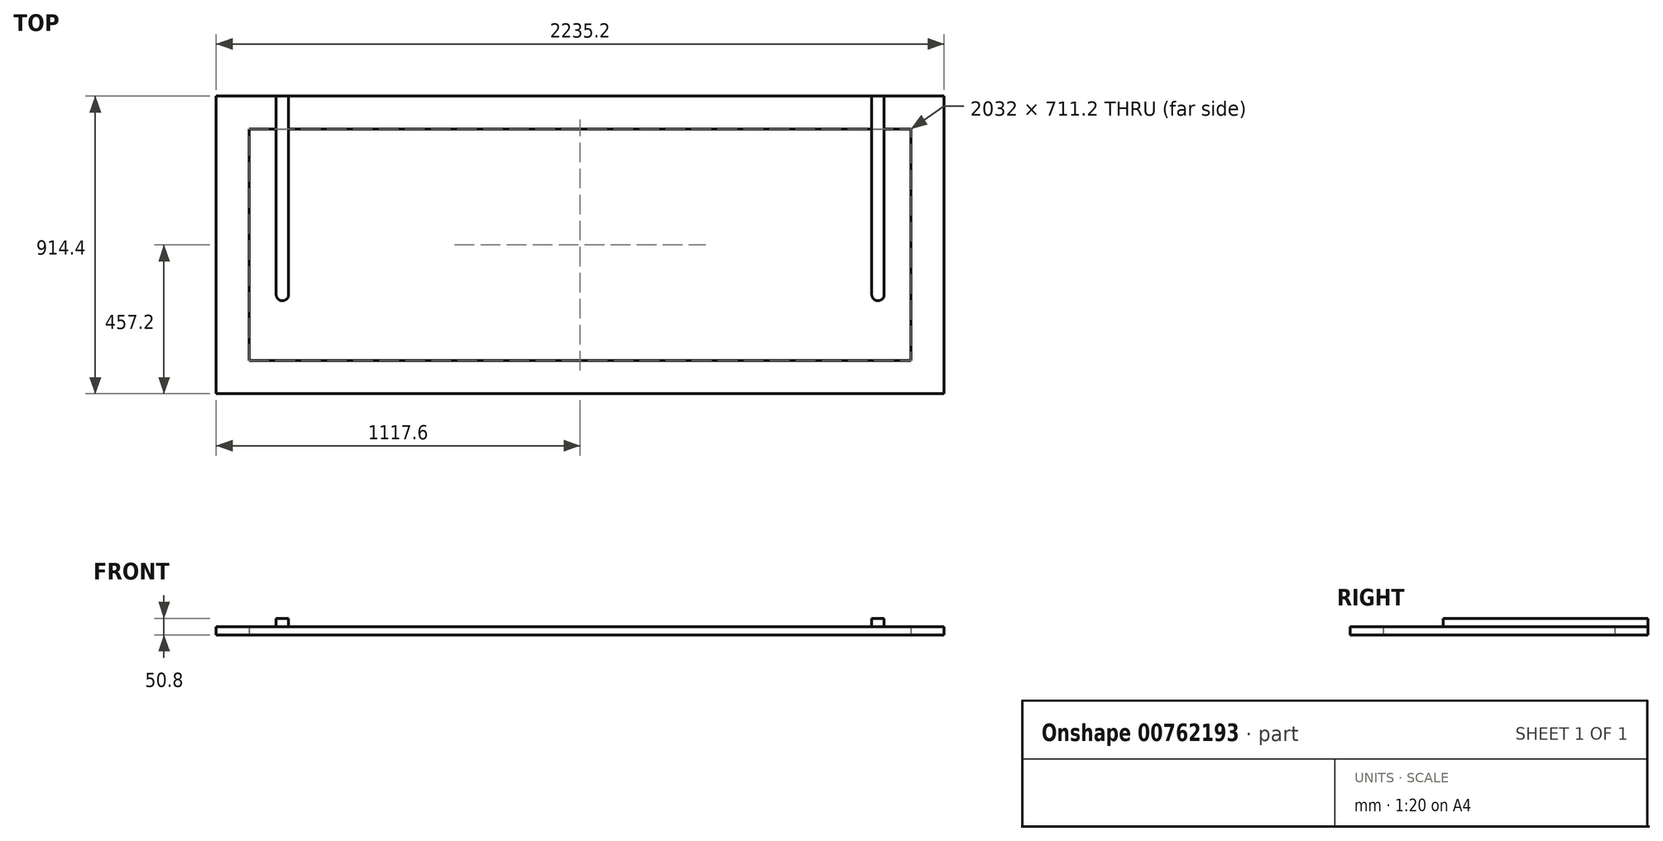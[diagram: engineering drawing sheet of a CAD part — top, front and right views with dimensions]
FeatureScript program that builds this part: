
annotation { "Feature Type Name" : "Feature", "Feature Type Description" : "" }
export const myFeature = defineFeature(function(context is Context, id is Id, definition is map)
    precondition{}
    {
        {
            var Q0;
            Q0=qCreatedBy(makeId("Top.planeOp"),FACE);
            var sketch = newSketch(context, id + "F0", { "sketchPlane" : qUnion([Q0])});
            skLineSegment(sketch, "E0.bottom", {"start": v(0, 0) * mm, "end": v(2235.2, 0) * mm});
            skLineSegment(sketch, "E0.top", {"start": v(0, -914.4) * mm, "end": v(2235.2, -914.4) * mm});
            skLineSegment(sketch, "E0.left", {"start": v(0, 0) * mm, "end": v(0, -914.4) * mm});
            skLineSegment(sketch, "E0.right", {"start": v(2235.2, 0) * mm, "end": v(2235.2, -914.4) * mm});
            skLineSegment(sketch, "E1.bottom", {"start": v(101.6, -101.6) * mm, "end": v(2133.6, -101.6) * mm});
            skLineSegment(sketch, "E1.top", {"start": v(101.6, -812.8) * mm, "end": v(2133.6, -812.8) * mm});
            skLineSegment(sketch, "E1.left", {"start": v(101.6, -101.6) * mm, "end": v(101.6, -812.8) * mm});
            skLineSegment(sketch, "E1.right", {"start": v(2133.6, -101.6) * mm, "end": v(2133.6, -812.8) * mm});
            skSolve(sketch);
        }
        {
            var Q0;
            Q0=makeQuery(id+"F0.imprint","IMPRINT",FACE,{"disambiguationData":[TD([[makeQuery(id+"F0.imprint","IMPRINT",EDGE,{"derivedFrom":sQuery(id+"F0.wireOp",EDGE,"E0.bottom")}),-1.0]])]});
            extrude(context, id + "F1", {"entities" : qUnion([Q0]), "depth" : 25.4 * mm, "offsetDistance" : 25.4 * mm});
        }
        {
            var Q0;
            Q0=makeQuery(id+"F1.opExtrude","CAP_FACE",FACE,{"disambiguationData":[OSD([sQuery(id+"F0.wireOp",EDGE,"E0.bottom"),sQuery(id+"F0.wireOp",EDGE,"E0.top"),sQuery(id+"F0.wireOp",EDGE,"E0.left"),sQuery(id+"F0.wireOp",EDGE,"E0.right"),sQuery(id+"F0.wireOp",EDGE,"E1.bottom"),sQuery(id+"F0.wireOp",EDGE,"E1.top"),sQuery(id+"F0.wireOp",EDGE,"E1.left"),sQuery(id+"F0.wireOp",EDGE,"E1.right")])],"isStart":false});
            var sketch = newSketch(context, id + "F2", { "sketchPlane" : qUnion([Q0])});
            skLineSegment(sketch, "E2.bottom", {"start": v(184.15, 0) * mm, "end": v(222.25, 0) * mm});
            skLineSegment(sketch, "E2.top", {"start": v(184.15, -609.6) * mm, "end": v(222.25, -609.6) * mm});
            skLineSegment(sketch, "E2.left", {"start": v(184.15, 0) * mm, "end": v(184.15, -609.6) * mm});
            skLineSegment(sketch, "E2.right", {"start": v(222.25, 0) * mm, "end": v(222.25, -609.6) * mm});
            skLineSegment(sketch, "E3.bottom", {"start": v(2012.95, 0) * mm, "end": v(2051.05, 0) * mm});
            skLineSegment(sketch, "E3.top", {"start": v(2012.95, -609.6) * mm, "end": v(2051.05, -609.6) * mm});
            skLineSegment(sketch, "E3.left", {"start": v(2012.95, 0) * mm, "end": v(2012.95, -609.6) * mm});
            skLineSegment(sketch, "E3.right", {"start": v(2051.05, 0) * mm, "end": v(2051.05, -609.6) * mm});
            skCircle(sketch, "E4", {"center": v(203.2, -609.6) * mm, "radius": 19.05 * mm});
            skCircle(sketch, "E5", {"center": v(2032, -609.6) * mm, "radius": 19.05 * mm});
            skSolve(sketch);
        }
        {
            var Q0;
            Q0 = qSketchRegion(id + "F2", true);
            extrude(context, id + "F3", {"entities" : qUnion([Q0]), "depth" : 25.4 * mm, "offsetDistance" : 25.4 * mm});
        }
    });
